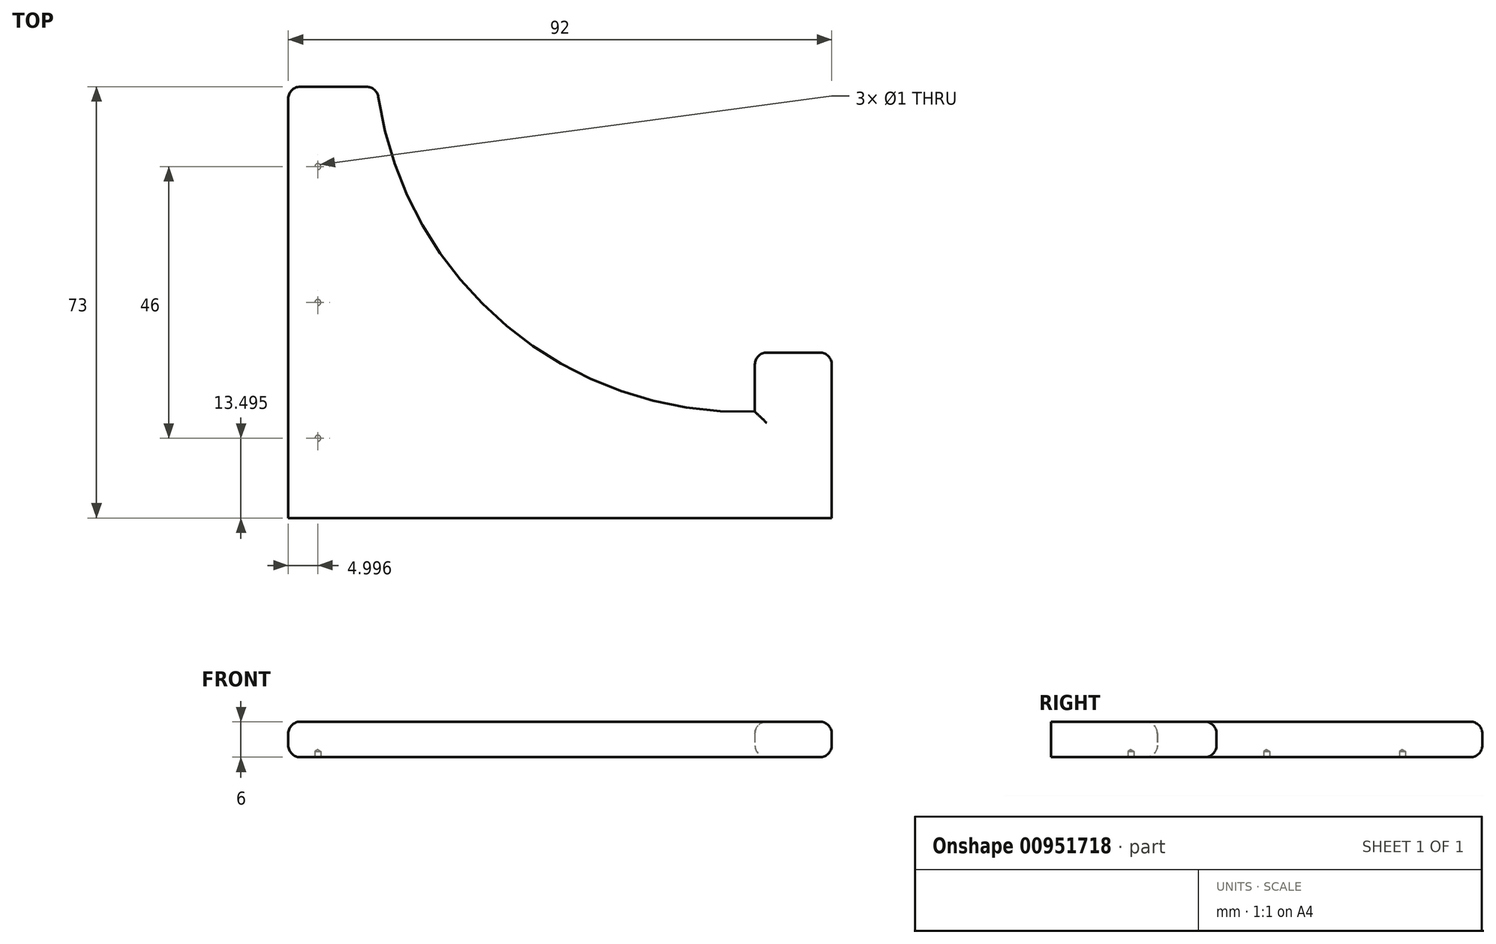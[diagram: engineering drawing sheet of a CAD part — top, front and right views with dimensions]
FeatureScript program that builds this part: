
annotation { "Feature Type Name" : "Feature", "Feature Type Description" : "" }
export const myFeature = defineFeature(function(context is Context, id is Id, definition is map)
    precondition{}
    {
        {
            var Q0;
            Q0=qCreatedBy(makeId("Top.planeOp"),FACE);
            var sketch = newSketch(context, id + "F0", { "sketchPlane" : qUnion([Q0])});
            skLineSegment(sketch, "E0.bottom", {"start": v(-43.17, -8.37) * mm, "end": v(48.83, -8.37) * mm});
            skLineSegment(sketch, "E0.top", {"start": v(-43.17, 64.63) * mm, "end": v(-28.17, 64.63) * mm});
            skLineSegment(sketch, "E0.left", {"start": v(-43.17, -8.37) * mm, "end": v(-43.17, 64.63) * mm});
            skLineSegment(sketch, "E0.right", {"start": v(48.83, -8.37) * mm, "end": v(48.83, 19.63) * mm});
            skLineSegment(sketch, "E1", {"start": v(35.83, 19.63) * mm, "end": v(48.83, 19.63) * mm});
            skLineSegment(sketch, "E2", {"start": v(35.83, 19.63) * mm, "end": v(35.83, 9.63) * mm});
            skArc(sketch, "E3", {"start": v(-28.17, 64.63) * mm, "mid": v(-6.85, 24.7) * mm, "end": v(35.83, 9.63) * mm});
            skSolve(sketch);
        }
        {
            var Q0;
            Q0=makeQuery(id+"F0.imprint","IMPRINT",FACE,{"disambiguationData":[TD([[makeQuery(id+"F0.imprint","IMPRINT",EDGE,{"derivedFrom":sQuery(id+"F0.wireOp",EDGE,"E0.bottom")}),1.0]])]});
            extrude(context, id + "F1", {"entities" : qUnion([Q0]), "depth" : 6 * mm, "offsetDistance" : 25 * mm});
        }
        {
            var Q0;
            Q0=makeQuery(id+"F1.opExtrude","CAP_FACE",FACE,{"disambiguationData":[OSD([sQuery(id+"F0.wireOp",EDGE,"E0.bottom"),sQuery(id+"F0.wireOp",EDGE,"E0.top"),sQuery(id+"F0.wireOp",EDGE,"E0.left"),sQuery(id+"F0.wireOp",EDGE,"E0.right"),sQuery(id+"F0.wireOp",EDGE,"E1"),sQuery(id+"F0.wireOp",EDGE,"E2"),sQuery(id+"F0.wireOp",EDGE,"E3")])],"isStart":true});
            var sketch = newSketch(context, id + "F2", { "sketchPlane" : qUnion([Q0])});
            skPoint(sketch, "E4", {"position": v(-38.17, -5.13) * mm});
            skPoint(sketch, "E5", {"position": v(-38.17, -28.13) * mm});
            skPoint(sketch, "E6", {"position": v(-38.17, -51.13) * mm});
            skPoint(sketch, "E7", {"position": v(-43.17, -28.13) * mm});
            skSolve(sketch);
        }
        {
            var Q0;
            Q0=sQuery(id+"F2.wireOp",VERTEX,"E4");
            var Q1;
            Q1=sQuery(id+"F2.wireOp",VERTEX,"E5");
            var Q2;
            Q2=sQuery(id+"F2.wireOp",VERTEX,"E6");
            var Q3;
            Q3=makeQuery(id+"F1.opExtrude","SWEPT_BODY",BODY,{"disambiguationData":[OSD([sQuery(id+"F0.wireOp",EDGE,"E0.bottom"),sQuery(id+"F0.wireOp",EDGE,"E0.top"),sQuery(id+"F0.wireOp",EDGE,"E0.left"),sQuery(id+"F0.wireOp",EDGE,"E0.right"),sQuery(id+"F0.wireOp",EDGE,"E1"),sQuery(id+"F0.wireOp",EDGE,"E2"),sQuery(id+"F0.wireOp",EDGE,"E3")])]});
            hole(context, id + "F3", {"style" : HoleStyle.SIMPLE, "endStyle" : HoleEndStyle.BLIND, "holeDiameter" : 1 * mm, "majorDiameter" : 5 * mm, "holeDepth" : 1 * mm, "isTappedThrough" : true, "tappedDepth" : 12 * mm, "tapClearance" : 3, "locations" : qUnion([Q0, Q1, Q2]), "scope" : qUnion([Q3])});
        }
        {
            var Q0;
            Q0=makeQuery(id+"F1.opExtrude","CAP_EDGE",EDGE,{"disambiguationData":[OSD([sQuery(id+"F0.wireOp",EDGE,"E0.right")])],"isStart":false});
            var Q1;
            Q1=makeQuery(id+"F1.opExtrude","CAP_EDGE",EDGE,{"disambiguationData":[OSD([sQuery(id+"F0.wireOp",EDGE,"E0.right")])],"isStart":true});
            var Q2;
            Q2=makeQuery(id+"F1.opExtrude","SWEPT_EDGE",EDGE,{"disambiguationData":[OSD([sQuery(id+"F0.wireOp",EDGE,"E0.right"),sQuery(id+"F0.wireOp",EDGE,"E1")])]});
            var Q3;
            Q3=makeQuery(id+"F1.opExtrude","CAP_EDGE",EDGE,{"disambiguationData":[OSD([sQuery(id+"F0.wireOp",EDGE,"E1")])],"isStart":true});
            var Q4;
            Q4=makeQuery(id+"F1.opExtrude","CAP_EDGE",EDGE,{"disambiguationData":[OSD([sQuery(id+"F0.wireOp",EDGE,"E1")])],"isStart":false});
            var Q5;
            Q5=makeQuery(id+"F1.opExtrude","SWEPT_EDGE",EDGE,{"disambiguationData":[OSD([sQuery(id+"F0.wireOp",EDGE,"E1"),sQuery(id+"F0.wireOp",EDGE,"E2")])]});
            var Q6;
            Q6=makeQuery(id+"F1.opExtrude","CAP_EDGE",EDGE,{"disambiguationData":[OSD([sQuery(id+"F0.wireOp",EDGE,"E2")])],"isStart":false});
            var Q7;
            Q7=makeQuery(id+"F1.opExtrude","CAP_EDGE",EDGE,{"disambiguationData":[OSD([sQuery(id+"F0.wireOp",EDGE,"E2")])],"isStart":true});
            var Q8;
            Q8=makeQuery(id+"F1.opExtrude","CAP_EDGE",EDGE,{"disambiguationData":[OSD([sQuery(id+"F0.wireOp",EDGE,"E3")])],"isStart":true});
            var Q9;
            Q9=makeQuery(id+"F1.opExtrude","CAP_EDGE",EDGE,{"disambiguationData":[OSD([sQuery(id+"F0.wireOp",EDGE,"E3")])],"isStart":false});
            var Q10;
            Q10=makeQuery(id+"F1.opExtrude","CAP_EDGE",EDGE,{"disambiguationData":[OSD([sQuery(id+"F0.wireOp",EDGE,"E0.top")])],"isStart":true});
            var Q11;
            Q11=makeQuery(id+"F1.opExtrude","CAP_EDGE",EDGE,{"disambiguationData":[OSD([sQuery(id+"F0.wireOp",EDGE,"E0.top")])],"isStart":false});
            var Q12;
            Q12=makeQuery(id+"F1.opExtrude","SWEPT_EDGE",EDGE,{"disambiguationData":[OSD([sQuery(id+"F0.wireOp",EDGE,"E0.top"),sQuery(id+"F0.wireOp",EDGE,"E0.left")])]});
            var Q13;
            Q13=makeQuery(id+"F1.opExtrude","CAP_EDGE",EDGE,{"disambiguationData":[OSD([sQuery(id+"F0.wireOp",EDGE,"E0.left")])],"isStart":true});
            var Q14;
            Q14=makeQuery(id+"F1.opExtrude","CAP_EDGE",EDGE,{"disambiguationData":[OSD([sQuery(id+"F0.wireOp",EDGE,"E0.left")])],"isStart":false});
            var Q15;
            Q15=makeQuery(id+"F1.opExtrude","SWEPT_EDGE",EDGE,{"disambiguationData":[OSD([sQuery(id+"F0.wireOp",EDGE,"E0.top"),sQuery(id+"F0.wireOp",EDGE,"E3")])]});
            fillet(context, id + "F4", {"entities" : qUnion([Q0, Q1, Q2, Q3, Q4, Q5, Q6, Q7, Q8, Q9, Q10, Q11, Q12, Q13, Q14, Q15]), "radius" : 2 * mm, "tangentPropagation" : true, "allowEdgeOverflow" : false});
        }
    });
